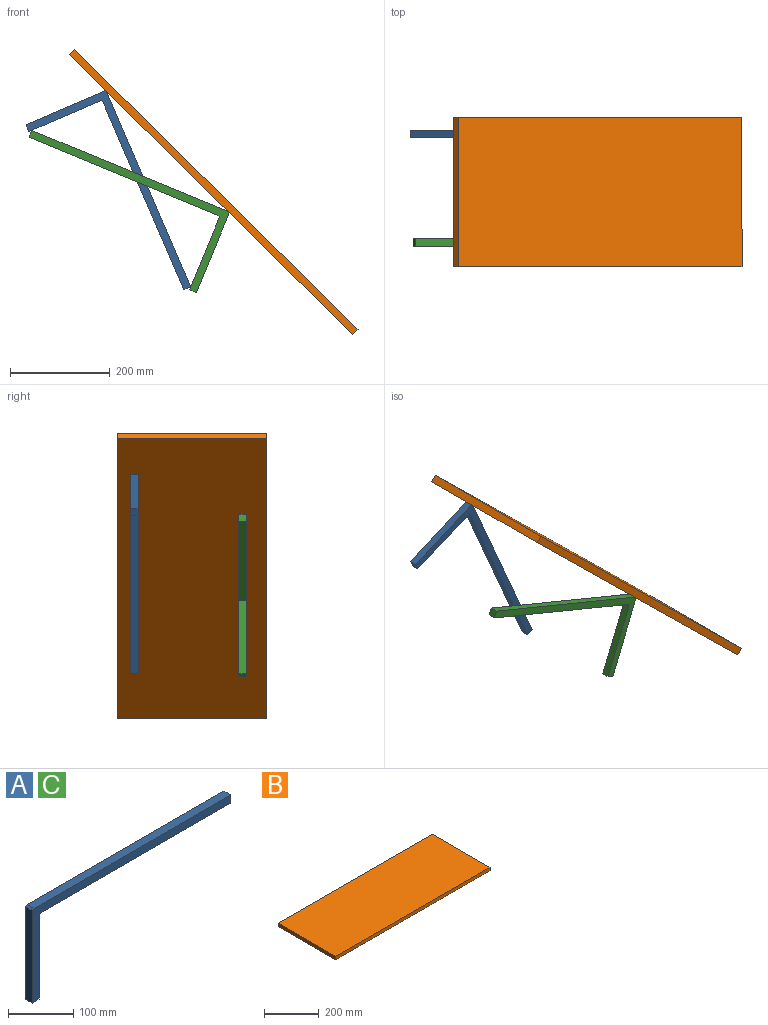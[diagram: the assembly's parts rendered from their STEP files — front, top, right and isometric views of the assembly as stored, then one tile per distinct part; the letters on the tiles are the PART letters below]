
ASSEMBLY  parts=3 mates=2
PART A: 10 faces, bbox 430x15x175 mm
  f0: plane 158.25x15mm, normal (1,0,0), area 2373.8mm2, adj f1,f7,f8,f9
  f1: plane 15x4.3mm, normal (0.38,0,-0.93), area 69.6mm2, adj f0,f2,f8,f9
  f2: plane 410.7x15mm, normal (0,0,-1), area 6160.5mm2, adj f1,f3,f8,f9
  f3: plane 15x15mm, normal (1,0,0), area 225mm2, adj f2,f4,f8,f9
  f4: plane 425.7x15mm, normal (0,0,1), area 6385.5mm2, adj f3,f5,f8,f9
  f5: plane 15x4.3mm, normal (-0.38,0,0.93), area 69.6mm2, adj f4,f6,f8,f9
  f6: plane 173.25x15mm, normal (-1,0,0), area 2598.7mm2, adj f5,f7,f8,f9
  f7: plane 15x15mm, normal (0,0,-1), area 225mm2, adj f0,f6,f8,f9
  f8: plane 430x175mm, normal (0,-1,0), area 8850mm2, adj f0,f1,f2,f3,f4,f5,f6,f7
  f9: plane 430x175mm, normal (0,1,0), area 8850mm2, adj f0,f1,f2,f3,f4,f5,f6,f7
PART B: 6 faces, bbox 800x300x15 mm
  f0: plane 800x15mm, normal (0,1,0), area 12000mm2, adj f1,f3,f4,f5
  f1: plane 300x15mm, normal (-1,0,0), area 4500mm2, adj f0,f2,f4,f5
  f2: plane 800x15mm, normal (0,-1,0), area 12000mm2, adj f1,f3,f4,f5
  f3: plane 300x15mm, normal (1,0,0), area 4500mm2, adj f0,f2,f4,f5
  f4: plane 800x300mm, normal (0,0,1), area 240000mm2, adj f0,f1,f2,f3
  f5: plane 800x300mm, normal (0,0,-1), area 240000mm2, adj f0,f1,f2,f3
PART C: same geometry as A
PLACE A rot(axis=(0,1,0),66.7deg) t=(239.11,320.78,165.9)mm
PLACE B rot(axis=(0,1,0),44.6deg) t=(325.67,47.28,305.87)mm
PLACE C rot(axis=(0.19,0,0.98),180deg) t=(581.72,88.19,-171.45)mm
MATE planar A.f5 <-> B.f5  axis (0.7,0,0.71) through (399.88,313.28,232.79)mm
MATE planar C.f5 <-> B.f5  axis (0.7,0,0.71) through (646.11,95.69,-9.66)mm
